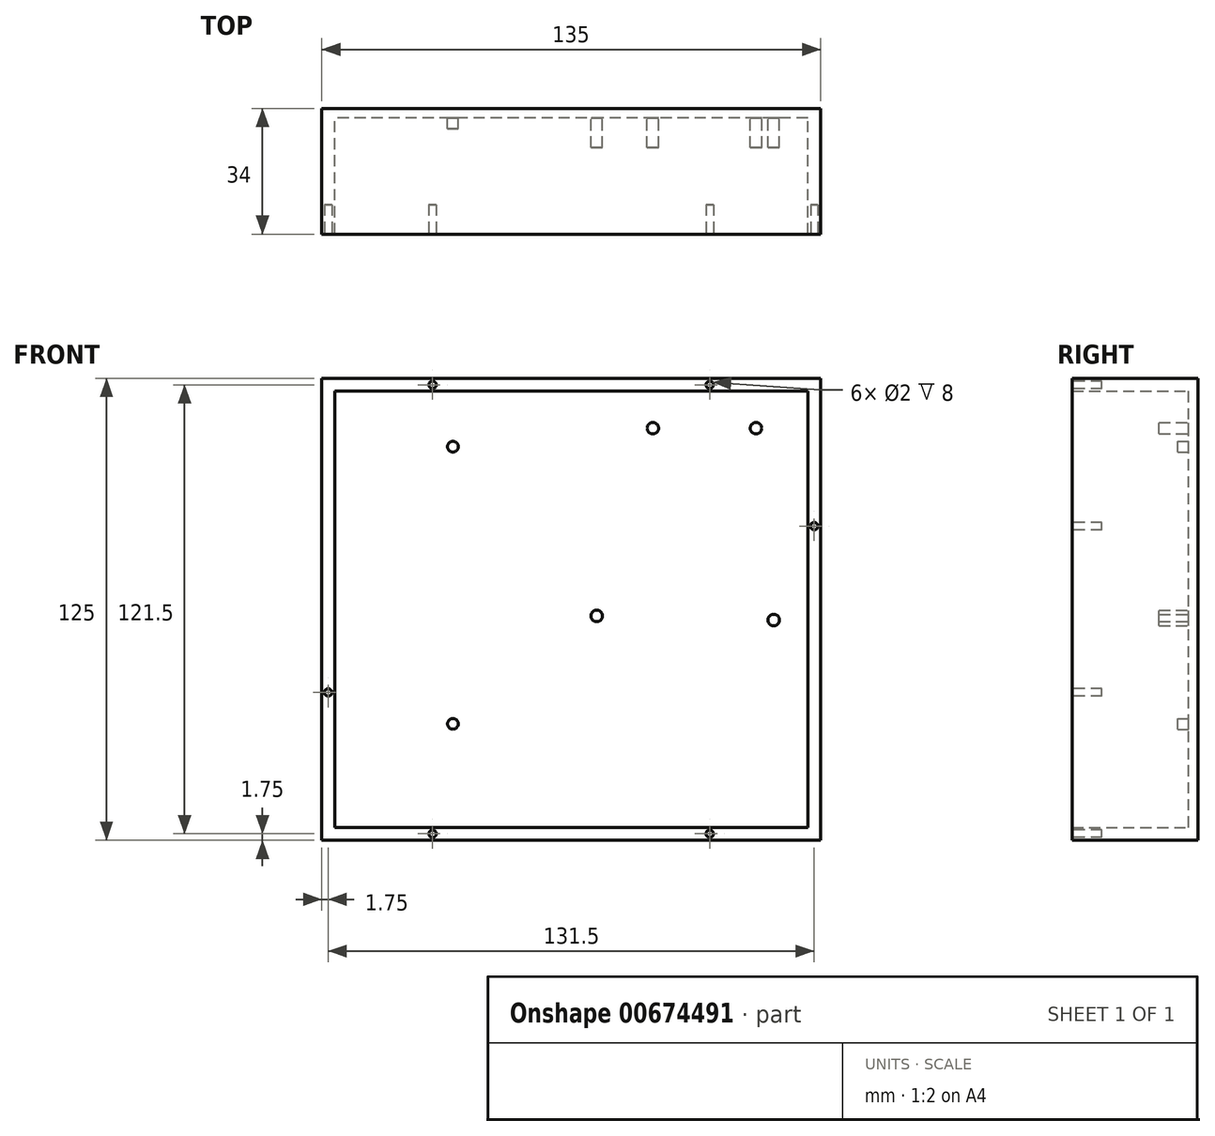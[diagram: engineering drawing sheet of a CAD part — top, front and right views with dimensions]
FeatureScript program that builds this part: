
annotation { "Feature Type Name" : "Feature", "Feature Type Description" : "" }
export const myFeature = defineFeature(function(context is Context, id is Id, definition is map)
    precondition{}
    {
        {
            var Q0;
            Q0=qCreatedBy(makeId("Front.planeOp"),FACE);
            var sketch = newSketch(context, id + "F0", { "sketchPlane" : qUnion([Q0])});
            skLineSegment(sketch, "E0.bottom", {"start": v(0, 0) * mm, "end": v(-135, 0) * mm});
            skLineSegment(sketch, "E0.top", {"start": v(0, 125) * mm, "end": v(-135, 125) * mm});
            skLineSegment(sketch, "E0.left", {"start": v(0, 0) * mm, "end": v(0, 125) * mm});
            skLineSegment(sketch, "E0.right", {"start": v(-135, 0) * mm, "end": v(-135, 125) * mm});
            skSolve(sketch);
        }
        {
            var Q0;
            Q0 = qSketchRegion(id + "F0", true);
            extrude(context, id + "F1", {"entities" : qUnion([Q0]), "depth" : 35 * mm, "offsetDistance" : 25 * mm});
        }
        {
            var Q0;
            Q0=makeQuery(id+"F1.opExtrude","CAP_FACE",FACE,{"disambiguationData":[OSD([sQuery(id+"F0.wireOp",EDGE,"E0.bottom"),sQuery(id+"F0.wireOp",EDGE,"E0.top"),sQuery(id+"F0.wireOp",EDGE,"E0.left"),sQuery(id+"F0.wireOp",EDGE,"E0.right")])],"isStart":false});
            shell(context, id + "F2", {"entities" : qUnion([Q0]), "thickness" : 3.5 * mm});
        }
        {
            var Q0;
            Q0=makeQuery(id+"F2.opShell","OFFSET_FACE",FACE,{"disambiguationData":[OSD([sQuery(id+"F0.wireOp",EDGE,"E0.bottom"),sQuery(id+"F0.wireOp",EDGE,"E0.top"),sQuery(id+"F0.wireOp",EDGE,"E0.left"),sQuery(id+"F0.wireOp",EDGE,"E0.right")])]});
            var sketch = newSketch(context, id + "F3", { "sketchPlane" : qUnion([Q0])});
            skCircle(sketch, "E1", {"center": v(-99.5, 106.5) * mm, "radius": 1.45 * mm});
            skCircle(sketch, "E2", {"center": v(-99.5, 31.5) * mm, "radius": 1.45 * mm});
            skCircle(sketch, "E3", {"center": v(-45.4, 111.5) * mm, "radius": 1.55 * mm});
            skCircle(sketch, "E4", {"center": v(-17.5, 111.5) * mm, "radius": 1.55 * mm});
            skCircle(sketch, "E5", {"center": v(-12.7, 59.6) * mm, "radius": 1.55 * mm});
            skCircle(sketch, "E6", {"center": v(-60.6, 60.7) * mm, "radius": 1.55 * mm});
            skSolve(sketch);
        }
        {
            var Q0;
            Q0 = qSketchRegion(id + "F3", true);
            extrude(context, id + "F4", {"entities" : qUnion([Q0]), "operationType" : NewBodyOperationType.ADD, "depth" : 8 * mm, "offsetDistance" : 25 * mm});
        }
        {
            var Q0;
            Q0=makeQuery(id+"F1.opExtrude","CAP_FACE",FACE,{"disambiguationData":[OSD([sQuery(id+"F0.wireOp",EDGE,"E0.bottom"),sQuery(id+"F0.wireOp",EDGE,"E0.top"),sQuery(id+"F0.wireOp",EDGE,"E0.left"),sQuery(id+"F0.wireOp",EDGE,"E0.right")])],"isStart":false});
            var sketch = newSketch(context, id + "F5", { "sketchPlane" : qUnion([Q0])});
            skCircle(sketch, "E7", {"center": v(-30, 123.25) * mm, "radius": 1 * mm});
            skCircle(sketch, "E8", {"center": v(-1.75, 85) * mm, "radius": 1 * mm});
            skCircle(sketch, "E9", {"center": v(-30, 1.75) * mm, "radius": 1 * mm});
            skCircle(sketch, "E10", {"center": v(-105, 1.75) * mm, "radius": 1 * mm});
            skCircle(sketch, "E11", {"center": v(-133.25, 40) * mm, "radius": 1 * mm});
            skCircle(sketch, "E12", {"center": v(-105, 123.25) * mm, "radius": 1 * mm});
            skSolve(sketch);
        }
        {
            var Q0;
            Q0 = qSketchRegion(id + "F5", true);
            extrude(context, id + "F6", {"entities" : qUnion([Q0]), "operationType" : NewBodyOperationType.REMOVE, "oppositeDirection" : true, "depth" : 8 * mm, "offsetDistance" : 25 * mm});
        }
        {
            var Q0;
            Q0=makeQuery(id+"F1.opExtrude","CAP_FACE",FACE,{"disambiguationData":[OSD([sQuery(id+"F0.wireOp",EDGE,"E0.bottom"),sQuery(id+"F0.wireOp",EDGE,"E0.top"),sQuery(id+"F0.wireOp",EDGE,"E0.left"),sQuery(id+"F0.wireOp",EDGE,"E0.right")])],"isStart":true});
            var sketch = newSketch(context, id + "F7", { "sketchPlane" : qUnion([Q0])});
            skLineSegment(sketch, "E13.bottom", {"start": v(135, 125) * mm, "end": v(0, 125) * mm});
            skLineSegment(sketch, "E13.top", {"start": v(135, 0) * mm, "end": v(0, 0) * mm});
            skLineSegment(sketch, "E13.left", {"start": v(135, 125) * mm, "end": v(135, 0) * mm});
            skLineSegment(sketch, "E13.right", {"start": v(0, 125) * mm, "end": v(0, 0) * mm});
            skSolve(sketch);
        }
        {
            var Q0;
            Q0 = qSketchRegion(id + "F7", true);
            extrude(context, id + "F8", {"entities" : qUnion([Q0]), "operationType" : NewBodyOperationType.REMOVE, "oppositeDirection" : true, "depth" : 1 * mm, "offsetDistance" : 25 * mm});
        }
        {
            var Q0;
            Q0=makeQuery(id+"F4.opExtrude","CAP_FACE",FACE,{"disambiguationData":[OSD([sQuery(id+"F3.wireOp",EDGE,"E1")])],"isStart":false});
            var sketch = newSketch(context, id + "F9", { "sketchPlane" : qUnion([Q0])});
            skCircle(sketch, "E14", {"center": v(-99.5, 106.5) * mm, "radius": 1.83 * mm});
            skSolve(sketch);
        }
        {
            var Q0;
            Q0 = qSketchRegion(id + "F9", true);
            extrude(context, id + "F10", {"entities" : qUnion([Q0]), "operationType" : NewBodyOperationType.REMOVE, "oppositeDirection" : true, "depth" : 5 * mm, "offsetDistance" : 25 * mm});
        }
        {
            var Q0;
            Q0=makeQuery(id+"F4.opExtrude","CAP_FACE",FACE,{"disambiguationData":[OSD([sQuery(id+"F3.wireOp",EDGE,"E2")])],"isStart":false});
            var sketch = newSketch(context, id + "F11", { "sketchPlane" : qUnion([Q0])});
            skCircle(sketch, "E15", {"center": v(-99.5, 31.5) * mm, "radius": 2.79 * mm});
            skSolve(sketch);
        }
        {
            var Q0;
            Q0 = qSketchRegion(id + "F11", true);
            extrude(context, id + "F12", {"entities" : qUnion([Q0]), "operationType" : NewBodyOperationType.REMOVE, "oppositeDirection" : true, "depth" : 5 * mm, "offsetDistance" : 25 * mm});
        }
    });
